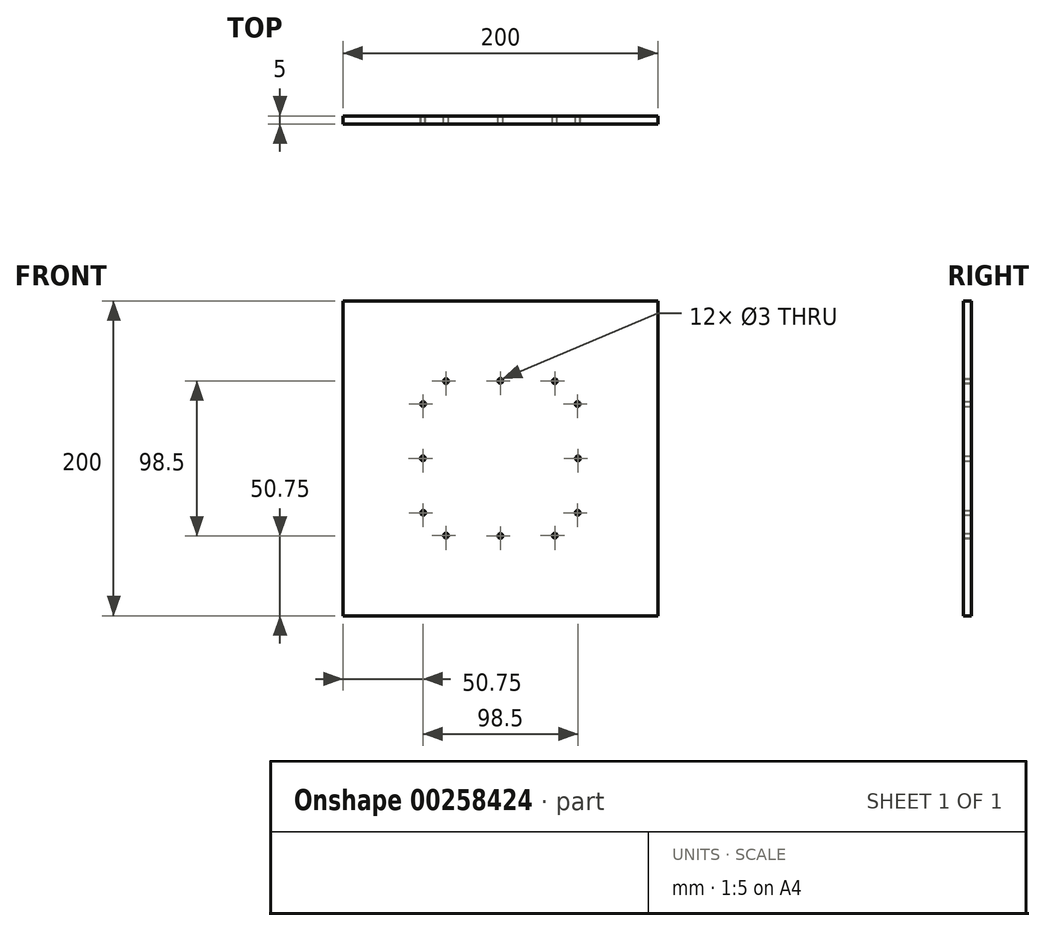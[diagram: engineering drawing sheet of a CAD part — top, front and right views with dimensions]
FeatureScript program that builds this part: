
annotation { "Feature Type Name" : "Feature", "Feature Type Description" : "" }
export const myFeature = defineFeature(function(context is Context, id is Id, definition is map)
    precondition{}
    {
        {
            var Q0;
            Q0=qCreatedBy(makeId("Front.planeOp"),FACE);
            var sketch = newSketch(context, id + "F0", { "sketchPlane" : qUnion([Q0])});
            skLineSegment(sketch, "E0.bottom", {"start": v(-100, 100) * mm, "end": v(100, 100) * mm});
            skLineSegment(sketch, "E0.top", {"start": v(-100, -100) * mm, "end": v(100, -100) * mm});
            skLineSegment(sketch, "E0.left", {"start": v(-100, 100) * mm, "end": v(-100, -100) * mm});
            skLineSegment(sketch, "E0.right", {"start": v(100, 100) * mm, "end": v(100, -100) * mm});
            skPoint(sketch, "E0.middle", {"position": v(0, 0) * mm});
            skCircle(sketch, "E1", {"center": v(0, 0) * mm, "radius": 49.25 * mm, "construction": true});
            skLineSegment(sketch, "E2", {"start": v(100, 0) * mm, "end": v(-100, 0) * mm, "construction": true});
            skLineSegment(sketch, "E3", {"start": v(0, -100) * mm, "end": v(0, 100) * mm, "construction": true});
            skPoint(sketch, "E3.startSnap0", {"position": v(0, -100) * mm});
            skCircle(sketch, "E4", {"center": v(49.25, 0) * mm, "radius": 1.5 * mm});
            skCircle(sketch, "E5.1.0", {"center": v(0, 49.25) * mm, "radius": 1.5 * mm});
            skCircle(sketch, "E5.2.0", {"center": v(-49.25, 0) * mm, "radius": 1.5 * mm});
            skCircle(sketch, "E5.3.0", {"center": v(0, -49.25) * mm, "radius": 1.5 * mm});
            skLineSegment(sketch, "E6", {"start": v(-100, 100) * mm, "end": v(100, -100) * mm, "construction": true});
            skLineSegment(sketch, "E7", {"start": v(-100, -100) * mm, "end": v(100, 100) * mm, "construction": true});
            skCircle(sketch, "E8", {"center": v(34.55, -49.05) * mm, "radius": 1.5 * mm});
            skCircle(sketch, "E9.MirrorC", {"center": v(49.05, -34.55) * mm, "radius": 1.5 * mm});
            skLineSegment(sketch, "E10.MirrorCS", {"start": v(100, 100) * mm, "end": v(-100, -100) * mm, "construction": true});
            skCircle(sketch, "E11.MirrorC", {"center": v(-34.55, 49.05) * mm, "radius": 1.5 * mm});
            skCircle(sketch, "E12.MirrorC", {"center": v(-49.05, 34.55) * mm, "radius": 1.5 * mm});
            skCircle(sketch, "E13", {"center": v(-49.05, -34.55) * mm, "radius": 1.5 * mm});
            skCircle(sketch, "E14.MirrorC", {"center": v(-34.55, -49.05) * mm, "radius": 1.5 * mm});
            skCircle(sketch, "E15.MirrorC", {"center": v(34.55, 49.05) * mm, "radius": 1.5 * mm});
            skCircle(sketch, "E16.MirrorC", {"center": v(49.05, 34.55) * mm, "radius": 1.5 * mm});
            skSolve(sketch);
        }
        {
            var Q0;
            Q0=makeQuery(id+"F0.imprint","IMPRINT",FACE,{"disambiguationData":[TD([[makeQuery(id+"F0.imprint","IMPRINT",EDGE,{"derivedFrom":sQuery(id+"F0.wireOp",EDGE,"E0.bottom")}),-1.0]])]});
            extrude(context, id + "F1", {"entities" : qUnion([Q0]), "depth" : 5 * mm});
        }
    });
